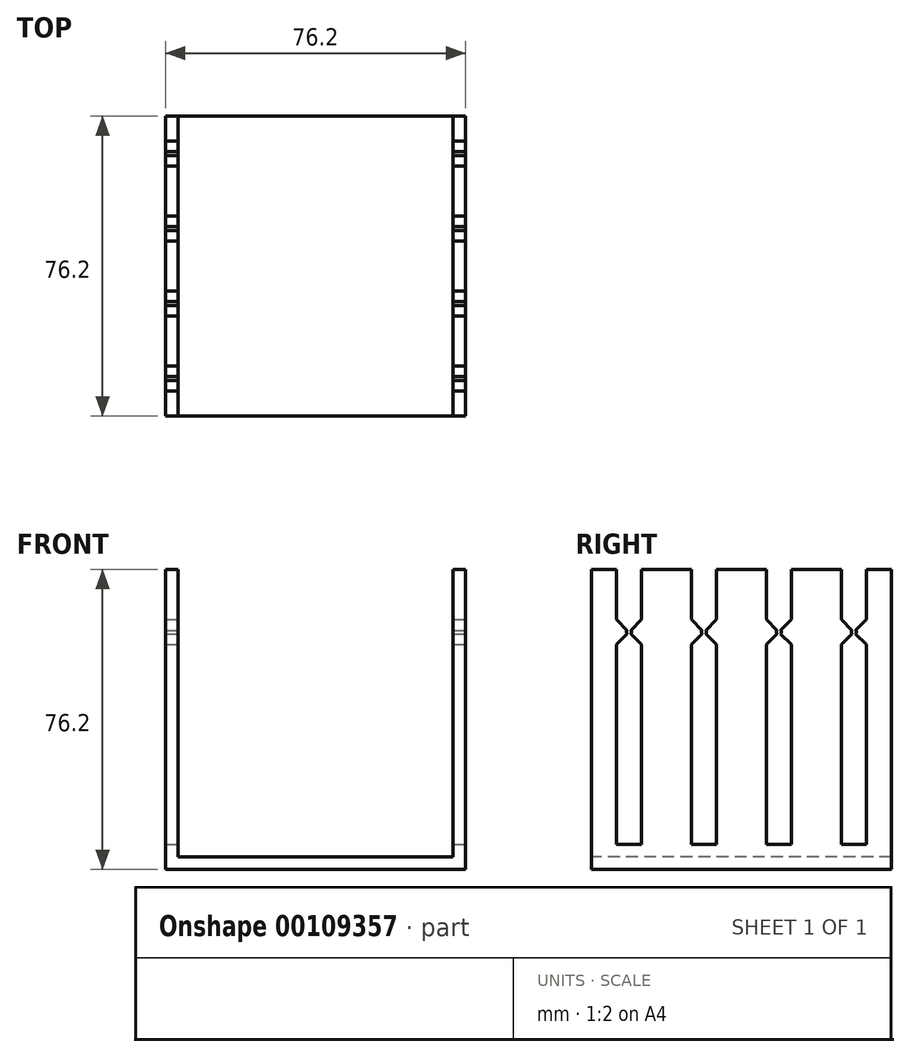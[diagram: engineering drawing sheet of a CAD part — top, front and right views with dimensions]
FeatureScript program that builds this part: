
annotation { "Feature Type Name" : "Feature", "Feature Type Description" : "" }
export const myFeature = defineFeature(function(context is Context, id is Id, definition is map)
    precondition{}
    {
        {
            var Q0;
            Q0=qCreatedBy(makeId("Top.planeOp"),FACE);
            var sketch = newSketch(context, id + "F0", { "sketchPlane" : qUnion([Q0])});
            skLineSegment(sketch, "E0.bottom", {"start": v(-38.1, 38.1) * mm, "end": v(38.1, 38.1) * mm});
            skLineSegment(sketch, "E0.top", {"start": v(-38.1, -38.1) * mm, "end": v(38.1, -38.1) * mm});
            skLineSegment(sketch, "E0.left", {"start": v(-38.1, 38.1) * mm, "end": v(-38.1, -38.1) * mm});
            skLineSegment(sketch, "E0.right", {"start": v(38.1, 38.1) * mm, "end": v(38.1, -38.1) * mm});
            skPoint(sketch, "E0.middle", {"position": v(0, 0) * mm});
            skSolve(sketch);
        }
        {
            var Q0;
            Q0 = qSketchRegion(id + "F0", true);
            extrude(context, id + "F1", {"entities" : qUnion([Q0]), "depth" : 76.2 * mm});
        }
        {
            var Q0;
            Q0=makeQuery(id+"F1.opExtrude","SWEPT_FACE",FACE,{"disambiguationData":[OSD([sQuery(id+"F0.wireOp",EDGE,"E0.right")])]});
            var sketch = newSketch(context, id + "F2", { "sketchPlane" : qUnion([Q0])});
            skLineSegment(sketch, "E1", {"start": v(-6.35, 76.2) * mm, "end": v(-6.35, 63.5) * mm});
            skLineSegment(sketch, "E2.MirrorCS", {"start": v(6.35, 76.2) * mm, "end": v(6.35, 63.5) * mm});
            skLineSegment(sketch, "E3.MirrorCS", {"start": v(12.7, 76.2) * mm, "end": v(12.7, 63.5) * mm});
            skLineSegment(sketch, "E4.MirrorCS", {"start": v(25.4, 76.2) * mm, "end": v(25.4, 63.5) * mm});
            skLineSegment(sketch, "E5.MirrorCS", {"start": v(-12.7, 76.2) * mm, "end": v(-12.7, 63.5) * mm});
            skLineSegment(sketch, "E6.MirrorCS", {"start": v(-25.4, 76.2) * mm, "end": v(-25.4, 63.5) * mm});
            skLineSegment(sketch, "E7.MirrorCS", {"start": v(-31.75, 76.2) * mm, "end": v(-31.75, 63.5) * mm});
            skLineSegment(sketch, "E8", {"start": v(-31.75, 63.5) * mm, "end": v(-29.02, 60.77) * mm});
            skLineSegment(sketch, "E9", {"start": v(-25.4, 63.5) * mm, "end": v(-28.13, 60.77) * mm});
            skLineSegment(sketch, "E10", {"start": v(-31.75, 57.15) * mm, "end": v(-31.75, 6.35) * mm});
            skLineSegment(sketch, "E11", {"start": v(-25.4, 57.15) * mm, "end": v(-25.4, 6.35) * mm});
            skLineSegment(sketch, "E12.MirrorCS", {"start": v(-12.7, 57.15) * mm, "end": v(-12.7, 6.35) * mm});
            skLineSegment(sketch, "E13.MirrorCS", {"start": v(-6.35, 57.15) * mm, "end": v(-6.35, 6.35) * mm});
            skLineSegment(sketch, "E14.MirrorCS", {"start": v(6.35, 57.15) * mm, "end": v(6.35, 6.35) * mm});
            skLineSegment(sketch, "E15.MirrorCS", {"start": v(12.7, 57.15) * mm, "end": v(12.7, 6.35) * mm});
            skLineSegment(sketch, "E16.MirrorCS", {"start": v(25.4, 57.15) * mm, "end": v(25.4, 6.35) * mm});
            skLineSegment(sketch, "E17.MirrorCS", {"start": v(31.75, 57.15) * mm, "end": v(31.75, 6.35) * mm});
            skPoint(sketch, "E18.MirrorCS.start.orphan", {"position": v(-6.35, 76.2) * mm});
            skLineSegment(sketch, "E19", {"start": v(31.75, 63.5) * mm, "end": v(31.75, 76.2) * mm});
            skLineSegment(sketch, "E20", {"start": v(-12.7, 63.5) * mm, "end": v(-9.97, 60.77) * mm});
            skLineSegment(sketch, "E21", {"start": v(-12.7, 57.15) * mm, "end": v(-9.97, 59.88) * mm});
            skLineSegment(sketch, "E22", {"start": v(6.35, 57.15) * mm, "end": v(9.08, 59.88) * mm});
            skLineSegment(sketch, "E23", {"start": v(12.7, 57.15) * mm, "end": v(9.97, 59.88) * mm});
            skLineSegment(sketch, "E24", {"start": v(25.4, 57.15) * mm, "end": v(28.13, 59.88) * mm});
            skLineSegment(sketch, "E25", {"start": v(25.4, 63.5) * mm, "end": v(28.13, 60.77) * mm});
            skLineSegment(sketch, "E26.trimOffspring", {"start": v(-9.08, 59.88) * mm, "end": v(-6.35, 57.15) * mm});
            skLineSegment(sketch, "E27.trimOffspring", {"start": v(-9.08, 60.77) * mm, "end": v(-6.35, 63.5) * mm});
            skArc(sketch, "E28", {"start": v(-28.13, 59.88) * mm, "mid": v(-27.94, 60.32) * mm, "end": v(-28.13, 60.77) * mm});
            skArc(sketch, "E29.trimOffspring", {"start": v(-29.02, 60.77) * mm, "mid": v(-29.21, 60.32) * mm, "end": v(-29.02, 59.88) * mm});
            skLineSegment(sketch, "E30.trimOffspring", {"start": v(-29.02, 59.88) * mm, "end": v(-31.75, 57.15) * mm});
            skLineSegment(sketch, "E31.trimOffspring", {"start": v(-28.13, 59.88) * mm, "end": v(-25.4, 57.15) * mm});
            skArc(sketch, "E32", {"start": v(-9.97, 60.77) * mm, "mid": v(-10.16, 60.33) * mm, "end": v(-9.97, 59.88) * mm});
            skArc(sketch, "E33.trimOffspring", {"start": v(-9.08, 59.88) * mm, "mid": v(-8.9, 60.32) * mm, "end": v(-9.08, 60.77) * mm});
            skArc(sketch, "E34", {"start": v(9.08, 60.77) * mm, "mid": v(8.89, 60.33) * mm, "end": v(9.08, 59.88) * mm});
            skArc(sketch, "E35.trimOffspring", {"start": v(9.97, 59.88) * mm, "mid": v(10.16, 60.32) * mm, "end": v(9.97, 60.77) * mm});
            skLineSegment(sketch, "E36.trimOffspring", {"start": v(9.08, 60.77) * mm, "end": v(6.35, 63.5) * mm});
            skLineSegment(sketch, "E37.trimOffspring", {"start": v(9.97, 60.77) * mm, "end": v(12.7, 63.5) * mm});
            skArc(sketch, "E38", {"start": v(28.13, 60.77) * mm, "mid": v(27.94, 60.33) * mm, "end": v(28.13, 59.88) * mm});
            skArc(sketch, "E39.trimOffspring", {"start": v(29.02, 59.88) * mm, "mid": v(29.21, 60.32) * mm, "end": v(29.02, 60.77) * mm});
            skLineSegment(sketch, "E40.trimOffspring", {"start": v(29.02, 59.88) * mm, "end": v(31.75, 57.15) * mm});
            skLineSegment(sketch, "E41.trimOffspring", {"start": v(29.02, 60.77) * mm, "end": v(31.75, 63.5) * mm});
            skLineSegment(sketch, "E42", {"start": v(-31.75, 6.35) * mm, "end": v(-25.4, 6.35) * mm});
            skLineSegment(sketch, "E43.trimOffspring", {"start": v(-12.7, 6.35) * mm, "end": v(-6.35, 6.35) * mm});
            skLineSegment(sketch, "E44.trimOffspring", {"start": v(6.35, 6.35) * mm, "end": v(12.7, 6.35) * mm});
            skLineSegment(sketch, "E45.trimOffspring", {"start": v(25.4, 6.35) * mm, "end": v(31.75, 6.35) * mm});
            skLineSegment(sketch, "E46", {"start": v(-31.75, 76.2) * mm, "end": v(-31.75, 85.5) * mm});
            skLineSegment(sketch, "E47", {"start": v(-31.75, 85.5) * mm, "end": v(31.63, 85.5) * mm});
            skLineSegment(sketch, "E48", {"start": v(31.75, 76.2) * mm, "end": v(31.63, 85.5) * mm});
            skLineSegment(sketch, "E49", {"start": v(12.7, 76.2) * mm, "end": v(25.4, 76.2) * mm});
            skLineSegment(sketch, "E50", {"start": v(6.35, 76.2) * mm, "end": v(-6.35, 76.2) * mm});
            skLineSegment(sketch, "E51", {"start": v(-12.7, 76.2) * mm, "end": v(-25.4, 76.2) * mm});
            skSolve(sketch);
        }
        {
            var Q0;
            {var subQ0=sQuery(id+"F2.wireOp",EDGE,"E6.MirrorCS");Q0=makeQuery(id+"F2.imprint","IMPRINT",FACE,{"disambiguationData":[TD([[makeQuery(id+"F2.imprint","IMPRINT",EDGE,{"derivedFrom":subQ0}),-1.0]])]});}
            var Q1;
            {var subQ0=sQuery(id+"F2.wireOp",EDGE,"E1");Q1=makeQuery(id+"F2.imprint","IMPRINT",FACE,{"disambiguationData":[TD([[makeQuery(id+"F2.imprint","IMPRINT",EDGE,{"derivedFrom":subQ0}),-1.0]])]});}
            var Q2;
            {var subQ1=sQuery(id+"F2.wireOp",EDGE,"E2.MirrorCS");Q2=makeQuery(id+"F2.imprint","IMPRINT",FACE,{"disambiguationData":[TD([[makeQuery(id+"F2.imprint","IMPRINT",EDGE,{"derivedFrom":subQ1}),1.0]])]});}
            var Q3;
            {var subQ0=sQuery(id+"F2.wireOp",EDGE,"E4.MirrorCS");Q3=makeQuery(id+"F2.imprint","IMPRINT",FACE,{"disambiguationData":[TD([[makeQuery(id+"F2.imprint","IMPRINT",EDGE,{"derivedFrom":subQ0}),1.0]])]});}
            var Q4;
            {var subQ5=sQuery(id+"F2.wireOp",EDGE,"E46");Q4=makeQuery(id+"F2.imprint","IMPRINT",FACE,{"disambiguationData":[TD([[makeQuery(id+"F2.imprint","IMPRINT",EDGE,{"derivedFrom":subQ5}),-1.0]])]});}
            extrude(context, id + "F3", {"entities" : qUnion([Q0, Q1, Q2, Q3, Q4]), "operationType" : NewBodyOperationType.REMOVE, "oppositeDirection" : true, "depth" : 131.88 * mm});
        }
        {
            var Q0;
            Q0=makeQuery(id+"F1.opExtrude","SWEPT_FACE",FACE,{"disambiguationData":[OSD([sQuery(id+"F0.wireOp",EDGE,"E0.top")])]});
            var sketch = newSketch(context, id + "F4", { "sketchPlane" : qUnion([Q0])});
            skLineSegment(sketch, "E52", {"start": v(-34.93, 3.18) * mm, "end": v(34.92, 3.18) * mm});
            skLineSegment(sketch, "E53", {"start": v(-34.93, 76.2) * mm, "end": v(-34.93, 3.17) * mm});
            skLineSegment(sketch, "E54", {"start": v(34.92, 76.2) * mm, "end": v(34.92, 3.17) * mm});
            skSolve(sketch);
        }
        {
            var Q0;
            Q0 = qSketchRegion(id + "F4", true);
            var Q1;
            Q1=makeQuery(id+"F4.imprint","IMPRINT",FACE,{"disambiguationData":[TD([[makeQuery(id+"F4.imprint","IMPRINT",EDGE,{"derivedFrom":sQuery(id+"F4.wireOp",EDGE,"E52")}),1.0]])]});
            extrude(context, id + "F5", {"entities" : qUnion([Q0, Q1]), "operationType" : NewBodyOperationType.REMOVE, "oppositeDirection" : true, "depth" : 151.5 * mm});
        }
    });
